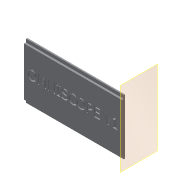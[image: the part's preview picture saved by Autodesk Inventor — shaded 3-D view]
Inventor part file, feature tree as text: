
AUTODESK INVENTOR PART (.ipt)
format: ipt  version: 2019 (Build 230136000, 136)  size: 355,328 bytes
history: native  units: mm
features: other x4, plane x2, sketch x2, extrude x2, reference x2
ambient origin geometry x8: Origin, YZ Plane, XZ Plane, XY Plane, X Axis, Y Axis, Z Axis, Center Point
bodies: Volumenkörper1 (feature_tree)
feature tree (12):
  plane  "Arbeitsebene1"
  sketch  "Skizze1"  dims[d5=10.0mm d6=0.0mm d14=1.0mm d15=0.0mm]
  plane  "Arbeitsebene2"
  other  "Arbeitspunkt1"
  extrude  "Extrusion1"  Depth=1.0mm TaperAngle=0.0deg
  extrude  "Extrusion3"  [1 undecoded]
  reference  "Referenz1"
  reference  "Referenz2"
  sketch  "Skizze3"
  other  "<userpath>\Documents\Inventor\HITscope\Assembly_Omniscope_v1.iam"
  other  "Assembly_Omniscope_v1.iam"
  other  "01_Camera_Module_left_v0:1"
note: 1 required parameter value undecoded (feature->parameter linkage not recoverable at this tier; creation-order binding heuristic only, values carry confidence <= 0.55)
